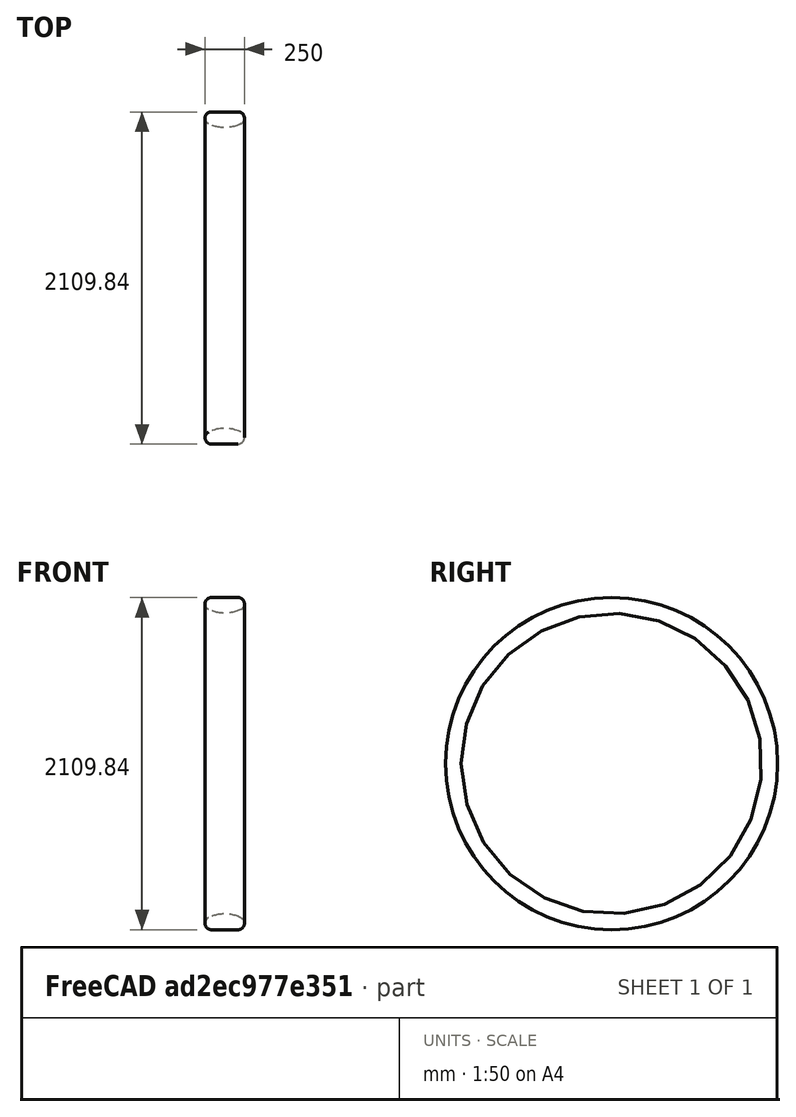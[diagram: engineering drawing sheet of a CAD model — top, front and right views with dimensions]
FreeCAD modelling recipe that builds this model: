
FCSTD DOCUMENT
Label: PR_008
objects: Sketcher::SketchObject×1, PartDesign::Revolution×1
note: 3 computed .brp shape members not serialized (recipe doc carries the construction recipe); baked Part::Feature solids carry a one-line shape summary decoded from their .brp

FEATURE [Sketcher::SketchObject] Sketch
  sketch-geometry (6):
    g0: LineSegment [constr] StartX=0 StartY=-954.92 StartZ=0 EndX=250 EndY=-954.92 EndZ=0
    g1: LineSegment StartX=40 StartY=-1054.92 StartZ=0 EndX=210 EndY=-1054.92 EndZ=0
    g2: ArcOfCircle CenterX=125 CenterY=-1185.55 CenterZ=0 NormalX=0 NormalY=0 NormalZ=1 Radius=230.625 StartAngle=1.10861 EndAngle=2.03298
    g3: ArcOfCircle CenterX=40 CenterY=-1014.92 CenterZ=0 NormalX=0 NormalY=0 NormalZ=1 Radius=40 StartAngle=2.03298 EndAngle=4.71239
    g4: ArcOfCircle CenterX=210 CenterY=-1014.92 CenterZ=0 NormalX=0 NormalY=0 NormalZ=1 Radius=40 StartAngle=4.71239 EndAngle=7.3918
    g5: LineSegment [constr] StartX=250 StartY=-954.92 StartZ=0 EndX=250 EndY=-1137.87 EndZ=0
  constraints (18):
    c: Horizontal(g0)
    c: DistanceY(g0) = -954.92
    c: Horizontal(g1)
    c: DistanceY(g1,g0) = 100
    c: Radius(g3) = 40
    c: Radius(g4) = 40
    c: Tangent(g3,g2)
    c: Tangent(g2,g4)
    c: Tangent(g3,g1)
    c: Tangent(g1,g4)
    c: Tangent(g2,g0)
    c: Tangent(g-2,g3)
    c: DistanceX(g0) = 0
    c: Vertical(g5)
    c: Coincident(g5,g0)
    c: Tangent(g5,g4)
    c: DistanceX(g5) = 250
    c: Distance(g5) = 182.954
FEATURE [PartDesign::Revolution] Revolution
  Angle = 360
  Axis = (1,0,0)
  Base = (0,0,0)
  ReferenceAxis = -> Sketch [H_Axis]
  Sketch = -> Sketch
